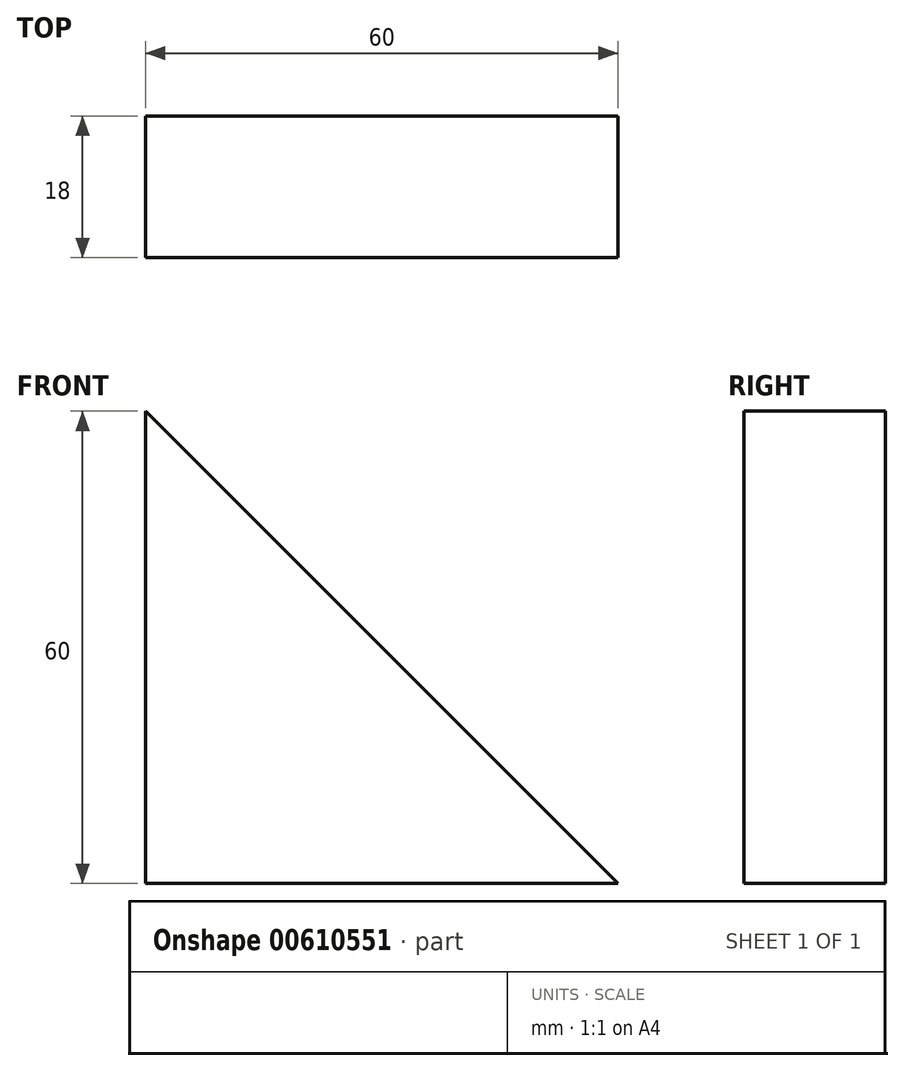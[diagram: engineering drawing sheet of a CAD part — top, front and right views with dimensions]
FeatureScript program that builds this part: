
annotation { "Feature Type Name" : "Feature", "Feature Type Description" : "" }
export const myFeature = defineFeature(function(context is Context, id is Id, definition is map)
    precondition{}
    {
        {
            var Q0;
            Q0=qCreatedBy(makeId("Front.planeOp"),FACE);
            var sketch = newSketch(context, id + "F0", { "sketchPlane" : qUnion([Q0])});
            skLineSegment(sketch, "E0", {"start": v(0, 0) * mm, "end": v(60, 0) * mm});
            skLineSegment(sketch, "E1", {"start": v(0, 0) * mm, "end": v(0, 60) * mm});
            skLineSegment(sketch, "E2", {"start": v(0, 60) * mm, "end": v(60, 0) * mm});
            skSolve(sketch);
        }
        {
            var Q0;
            Q0=makeQuery(id+"F0.imprint","IMPRINT",FACE,{"disambiguationData":[TD([[makeQuery(id+"F0.imprint","IMPRINT",EDGE,{"derivedFrom":sQuery(id+"F0.wireOp",EDGE,"E0")}),1.0]])]});
            extrude(context, id + "F1", {"entities" : qUnion([Q0]), "depth" : 18 * mm, "offsetDistance" : 25 * mm});
        }
    });
